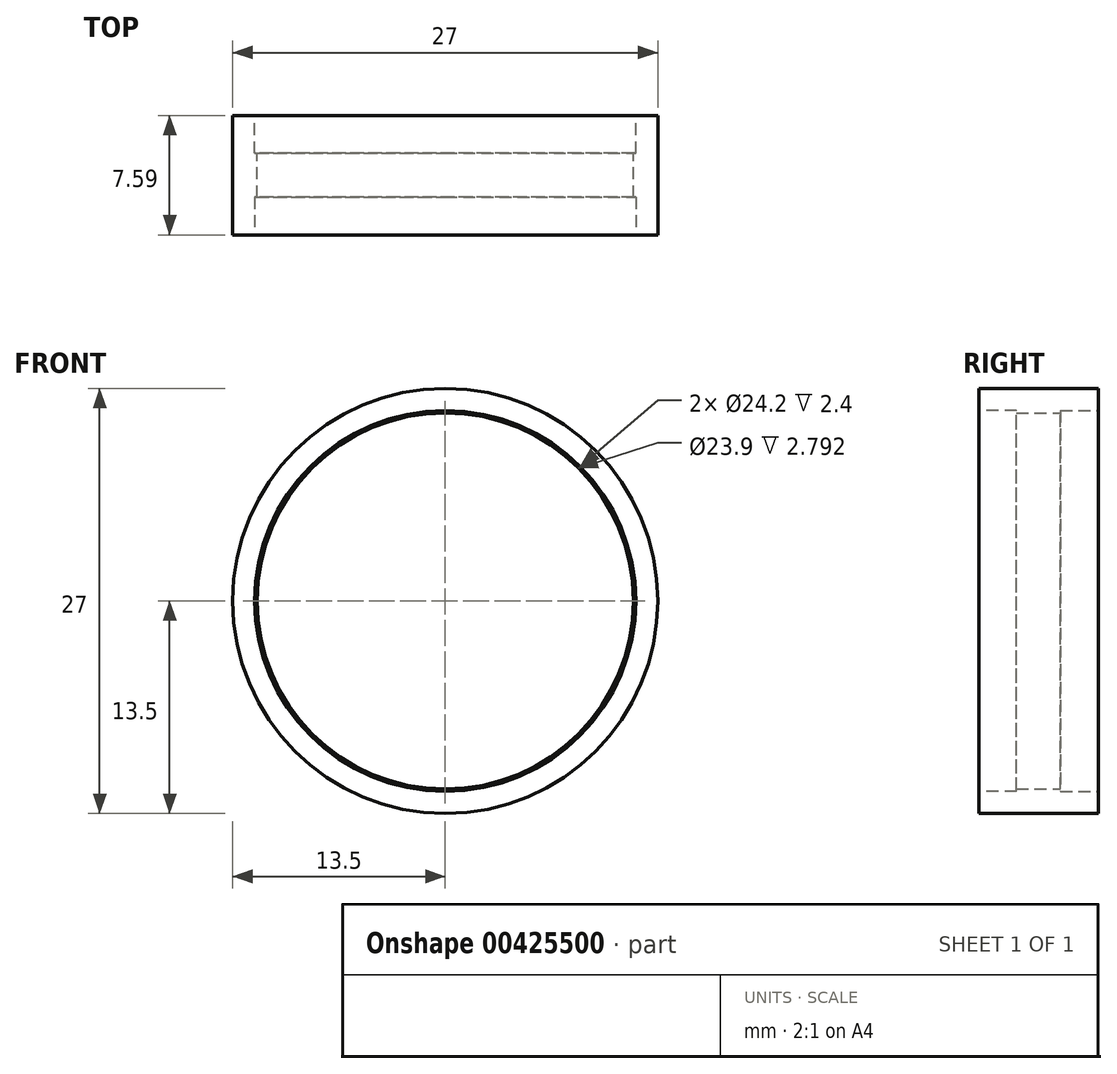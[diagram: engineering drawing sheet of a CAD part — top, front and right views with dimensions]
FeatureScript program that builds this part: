
annotation { "Feature Type Name" : "Feature", "Feature Type Description" : "" }
export const myFeature = defineFeature(function(context is Context, id is Id, definition is map)
    precondition{}
    {
        {
            var Q0;
            Q0=qCreatedBy(makeId("Front.planeOp"),FACE);
            var sketch = newSketch(context, id + "F0", { "sketchPlane" : qUnion([Q0])});
            skCircle(sketch, "E0", {"center": v(0, 0) * mm, "radius": 13.5 * mm});
            skCircle(sketch, "E1", {"center": v(0, 0) * mm, "radius": 11.95 * mm});
            skSolve(sketch);
        }
        {
            var Q0;
            Q0=makeQuery(id+"F0.imprint","IMPRINT",FACE,{"disambiguationData":[TD([[makeQuery(id+"F0.imprint","IMPRINT",EDGE,{"derivedFrom":sQuery(id+"F0.wireOp",EDGE,"E0")}),1.0]])]});
            extrude(context, id + "F1", {"entities" : qUnion([Q0]), "depth" : 7.2 / 2 * mm, "hasSecondDirection" : true, "secondDirectionOppositeDirection" : true, "secondDirectionDepth" : 4 * mm});
        }
        {
            var Q0;
            Q0=makeQuery(id+"F1.opExtrude","CAP_FACE",FACE,{"disambiguationData":[OSD([sQuery(id+"F0.wireOp",EDGE,"E0"),sQuery(id+"F0.wireOp",EDGE,"E1")])],"isStart":true});
            var sketch = newSketch(context, id + "F2", { "sketchPlane" : qUnion([Q0])});
            skCircle(sketch, "E2", {"center": v(0, 0) * mm, "radius": 12.1 * mm});
            skSolve(sketch);
        }
        {
            var Q0;
            Q0=makeQuery(id+"F2.imprint","IMPRINT",FACE,{"disambiguationData":[TD([[makeQuery(id+"F2.imprint","IMPRINT",EDGE,{"derivedFrom":sQuery(id+"F2.wireOp",EDGE,"E2")}),1.0]])]});
            extrude(context, id + "F3", {"entities" : qUnion([Q0]), "operationType" : NewBodyOperationType.REMOVE, "oppositeDirection" : true, "depth" : 2.4 * mm});
        }
        {
            var Q0;
            Q0=makeQuery(id+"F1.opExtrude","CAP_FACE",FACE,{"disambiguationData":[OSD([sQuery(id+"F0.wireOp",EDGE,"E0"),sQuery(id+"F0.wireOp",EDGE,"E1")])],"isStart":false});
            var sketch = newSketch(context, id + "F4", { "sketchPlane" : qUnion([Q0])});
            skCircle(sketch, "E3", {"center": v(0, 0) * mm, "radius": 12.1 * mm});
            skSolve(sketch);
        }
        {
            var Q0;
            Q0=makeQuery(id+"F4.imprint","IMPRINT",FACE,{"disambiguationData":[TD([[makeQuery(id+"F4.imprint","IMPRINT",EDGE,{"derivedFrom":sQuery(id+"F4.wireOp",EDGE,"E3")}),1.0]])]});
            extrude(context, id + "F5", {"entities" : qUnion([Q0]), "operationType" : NewBodyOperationType.REMOVE, "oppositeDirection" : true, "depth" : 2.4 * mm});
        }
    });
